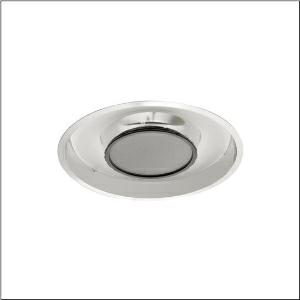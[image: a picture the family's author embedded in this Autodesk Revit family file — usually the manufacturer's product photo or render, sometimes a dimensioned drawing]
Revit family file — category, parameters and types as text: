
# Revit family: lunis_11_r_5lr610d4ob11af
name_source: partatom
category: Lighting Fixtures
units: mm (PartAtom-declared; Revit-internal decimal feet)

## family parameters
Cut with Voids When Loaded = No
Host = Face
Light Source = No
Part Type = Normal
Room Calculation Point = No
Round Connector Dimension = Use Diameter
Shared = No

## types (1)
- --- (1 x LED 4000K / CRI = 80 (unbekannt), 4860 lm, 4000K)
    Apparent Load = 37 VA
    CIE Flux Codes = 60 90 99 100 100
    Color Rendering = 80
    Color Temperature = 4000K
    Default Elevation = 1800 mm
    Description = Lunis 11 R, downlight, light control with reflector, of ultra-pure aluminium (Al 99.98%), highly specular, perforated, light emission: direct distribution, LED rated luminous flux: 4.860lm, light colour: 840, control gear: ECG Multilumen, with terminal, 3+2-pole, max. 2.5mm², mains connection: 230V, AC, 50/60Hz, diameter: 398mm, central ring, of plastic, graphite (RAL 7037), central module, blanking cover, of sheet steel, perforated, metallic grey (RAL 9006), protection rating (complete): IP20, insulation class (complete): insulation class II (safety insulation), certification: CE, ENEC, VDE, protection symbol: F, permissible ambient temperature for indoor applications: +10..+35°C, standard: EN 50419, packaging unit: 1 piece
    Height = 0 mm  [stored 0 ft]
    Lamp = 1 x LED 4000K / CRI >= 80 (unbekannt)
    Lamp Light Flux = 4860 lm
    Lamp count = 1
    Length = 398 mm
    Luminous efficacy = 131 lm/W
    Manufacturer = Siteco
    ModVariant = No
    Model = 5LR610D4OB11AF
    Mounting Place = Ceiling
    Mounting Type = Recessed
    Number of Poles = 1
    OnlyDefault = Yes
    Power Factor = 1
    Product Name = Lunis 11 R
    Product group = downlight
    ProductGroupID = 400
    Protection Class = Protection class II
    Protection Degree = IP 20
    RLX_Detail_Level = 1
    RLX_Emergency_Light_Flux = 0 lm
    RLX_Emergency_Type = 0
    RLX_Emergency_Type_DB = No
    RlxData = <blob elided: 94345 chars, md5=b4669ea4>
    Socket = socket
    Standby Power = 0 W
    System Light Flux = 4860 lm
    System Power = 37 W
    Type Comments = factory setting: High Lumen Output
    Type Image = l_1003323.jpg
    URL = http://relux.com
    VarID = @adj_164473
    Voltage = 0 V
    Weight = 0.00 kg
    Width = 0 mm  [stored 0 ft]

note: [stored X ft] marks values corroborated as IEEE doubles in the binary element streams (Revit-internal decimal feet)

## geometry (parser evidence)
native form markers: Blend x4, Sweep x10
no freeform markers — native parametric forms only
